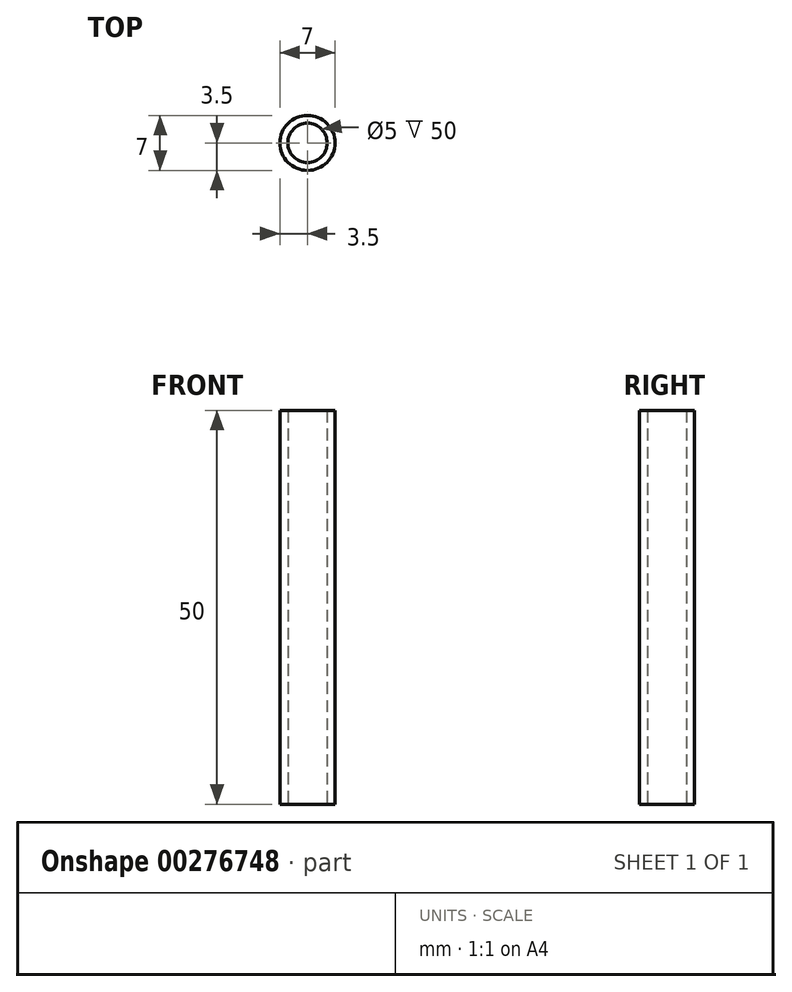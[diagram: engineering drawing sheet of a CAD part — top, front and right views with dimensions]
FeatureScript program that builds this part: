
annotation { "Feature Type Name" : "Feature", "Feature Type Description" : "" }
export const myFeature = defineFeature(function(context is Context, id is Id, definition is map)
    precondition{}
    {
        {
            var Q0;
            Q0=qCreatedBy(makeId("Top.planeOp"),FACE);
            var sketch = newSketch(context, id + "F0", { "sketchPlane" : qUnion([Q0])});
            skCircle(sketch, "E0", {"center": v(0, 0) * mm, "radius": 2.5 * mm});
            skCircle(sketch, "E1", {"center": v(0, 0) * mm, "radius": 3.5 * mm});
            skSolve(sketch);
        }
        {
            var Q0;
            Q0 = qSketchRegion(id + "F0", true);
            extrude(context, id + "F1", {"entities" : qUnion([Q0]), "depth" : 50 * mm});
        }
    });
